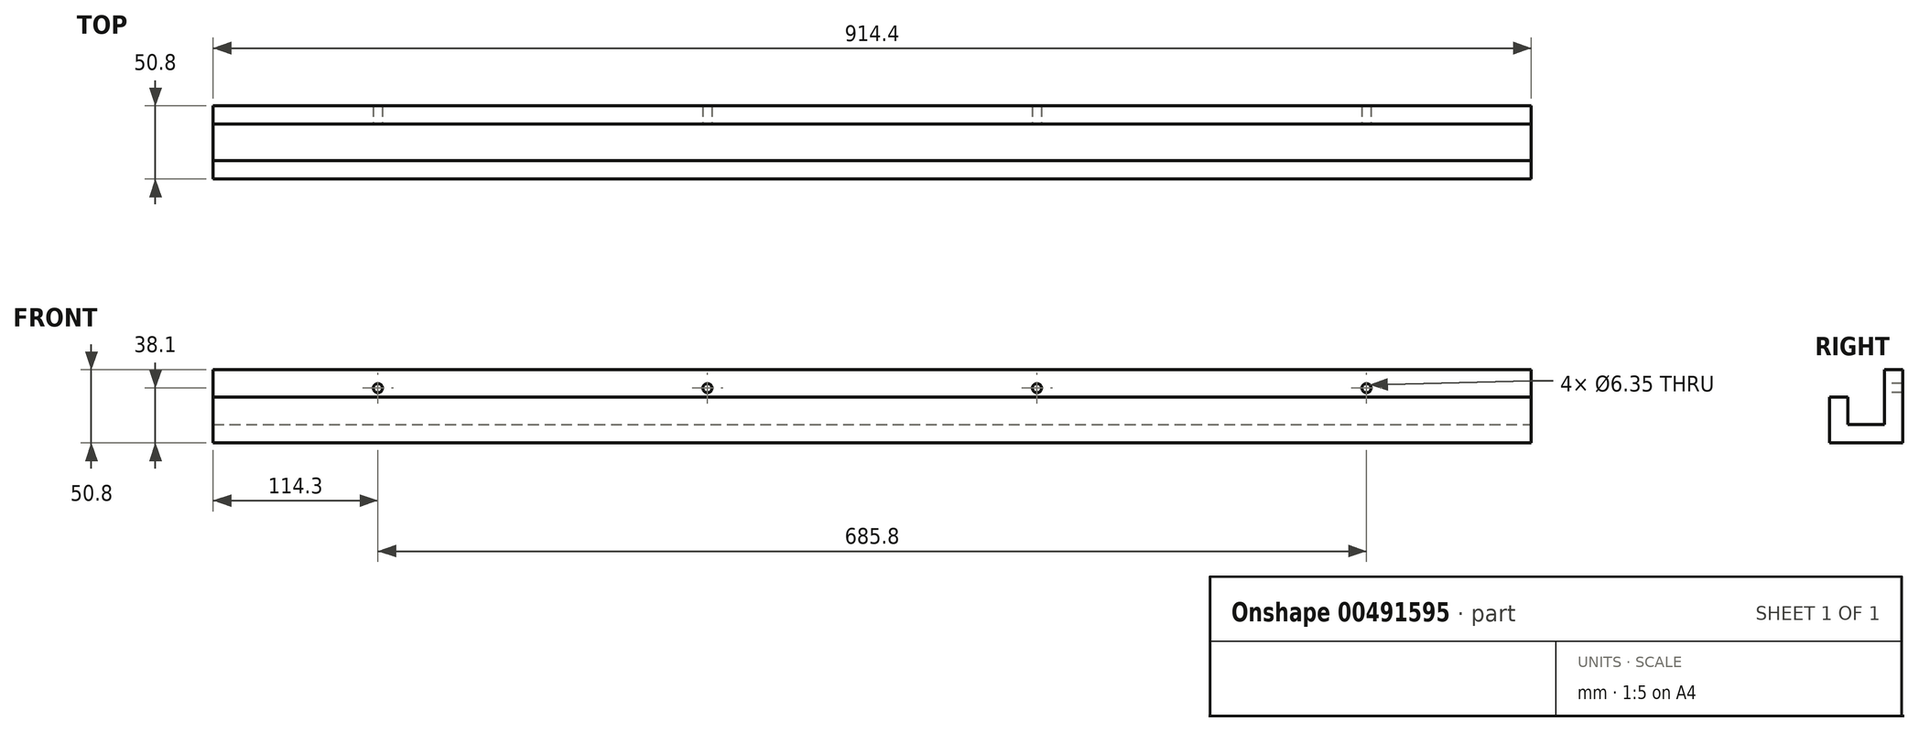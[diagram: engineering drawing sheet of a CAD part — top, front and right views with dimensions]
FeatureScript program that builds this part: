
annotation { "Feature Type Name" : "Feature", "Feature Type Description" : "" }
export const myFeature = defineFeature(function(context is Context, id is Id, definition is map)
    precondition{}
    {
        {
            var Q0;
            Q0=qCreatedBy(makeId("Front.planeOp"),FACE);
            var sketch = newSketch(context, id + "F0", { "sketchPlane" : qUnion([Q0])});
            skLineSegment(sketch, "E0.bottom", {"start": v(457.2, 25.4) * mm, "end": v(-457.2, 25.4) * mm});
            skLineSegment(sketch, "E0.top", {"start": v(457.2, -25.4) * mm, "end": v(-457.2, -25.4) * mm});
            skLineSegment(sketch, "E0.left", {"start": v(457.2, 25.4) * mm, "end": v(457.2, -25.4) * mm});
            skLineSegment(sketch, "E0.right", {"start": v(-457.2, 25.4) * mm, "end": v(-457.2, -25.4) * mm});
            skPoint(sketch, "E0.middle", {"position": v(0, 0) * mm});
            skSolve(sketch);
        }
        {
            var Q0;
            Q0=makeQuery(id+"F0.imprint","IMPRINT",FACE,{"disambiguationData":[TD([[makeQuery(id+"F0.imprint","IMPRINT",EDGE,{"derivedFrom":sQuery(id+"F0.wireOp",EDGE,"E0.bottom")}),1.0]])]});
            extrude(context, id + "F1", {"entities" : qUnion([Q0]), "depth" : 12.7 * mm});
        }
        {
            var Q0;
            Q0=makeQuery(id+"F1.opExtrude","CAP_FACE",FACE,{"disambiguationData":[OSD([sQuery(id+"F0.wireOp",EDGE,"E0.bottom"),sQuery(id+"F0.wireOp",EDGE,"E0.top"),sQuery(id+"F0.wireOp",EDGE,"E0.left"),sQuery(id+"F0.wireOp",EDGE,"E0.right")])],"isStart":false});
            var sketch = newSketch(context, id + "F2", { "sketchPlane" : qUnion([Q0])});
            skLineSegment(sketch, "E1.bottom", {"start": v(-457.2, -25.4) * mm, "end": v(457.2, -25.4) * mm});
            skLineSegment(sketch, "E1.top", {"start": v(-457.2, -12.7) * mm, "end": v(457.2, -12.7) * mm});
            skLineSegment(sketch, "E1.left", {"start": v(-457.2, -25.4) * mm, "end": v(-457.2, -12.7) * mm});
            skLineSegment(sketch, "E1.right", {"start": v(457.2, -25.4) * mm, "end": v(457.2, -12.7) * mm});
            skSolve(sketch);
        }
        {
            var Q0;
            Q0=makeQuery(id+"F2.imprint","IMPRINT",FACE,{"disambiguationData":[TD([[makeQuery(id+"F2.imprint","IMPRINT",EDGE,{"derivedFrom":sQuery(id+"F2.wireOp",EDGE,"E1.bottom")}),-1.0]])]});
            extrude(context, id + "F3", {"entities" : qUnion([Q0]), "operationType" : NewBodyOperationType.ADD, "depth" : 38.1 * mm});
        }
        {
            var Q0;
            Q0=makeQuery(id+"F3.opExtrude","SWEPT_FACE",FACE,{"disambiguationData":[OSD([sQuery(id+"F2.wireOp",EDGE,"E1.top")])]});
            var sketch = newSketch(context, id + "F4", { "sketchPlane" : qUnion([Q0])});
            skLineSegment(sketch, "E2.bottom", {"start": v(-457.2, -50.8) * mm, "end": v(457.2, -50.8) * mm});
            skLineSegment(sketch, "E2.top", {"start": v(-457.2, -38.1) * mm, "end": v(457.2, -38.1) * mm});
            skLineSegment(sketch, "E2.left", {"start": v(-457.2, -50.8) * mm, "end": v(-457.2, -38.1) * mm});
            skLineSegment(sketch, "E2.right", {"start": v(457.2, -50.8) * mm, "end": v(457.2, -38.1) * mm});
            skSolve(sketch);
        }
        {
            var Q0;
            Q0=makeQuery(id+"F4.imprint","IMPRINT",FACE,{"disambiguationData":[TD([[makeQuery(id+"F4.imprint","IMPRINT",EDGE,{"derivedFrom":sQuery(id+"F4.wireOp",EDGE,"E2.bottom")}),1.0]])]});
            extrude(context, id + "F5", {"entities" : qUnion([Q0]), "operationType" : NewBodyOperationType.ADD, "depth" : 19.05 * mm, "offsetDistance" : 25.4 * mm});
        }
        {
            var Q0;
            Q0=makeQuery(id+"F1.opExtrude","CAP_FACE",FACE,{"disambiguationData":[OSD([sQuery(id+"F0.wireOp",EDGE,"E0.bottom"),sQuery(id+"F0.wireOp",EDGE,"E0.top"),sQuery(id+"F0.wireOp",EDGE,"E0.left"),sQuery(id+"F0.wireOp",EDGE,"E0.right")])],"isStart":false});
            var sketch = newSketch(context, id + "F6", { "sketchPlane" : qUnion([Q0])});
            skCircle(sketch, "E3", {"center": v(-342.9, 12.7) * mm, "radius": 3.18 * mm});
            skCircle(sketch, "E4.1.0.0", {"center": v(-114.3, 12.7) * mm, "radius": 3.18 * mm});
            skCircle(sketch, "E4.2.0.0", {"center": v(114.3, 12.7) * mm, "radius": 3.18 * mm});
            skCircle(sketch, "E4.3.0.0", {"center": v(342.9, 12.7) * mm, "radius": 3.18 * mm});
            skLineSegment(sketch, "E4.direction1", {"start": v(-342.9, 12.7) * mm, "end": v(-114.3, 12.7) * mm, "construction": true});
            skSolve(sketch);
        }
        {
            var Q0;
            Q0=sQuery(id+"F6.wireOp",VERTEX,"E4.direction1.start");
            var Q1;
            Q1=sQuery(id+"F6.wireOp",VERTEX,"E4.1.0.0.center");
            var Q2;
            Q2=sQuery(id+"F6.wireOp",VERTEX,"E4.2.0.0.center");
            var Q3;
            Q3=sQuery(id+"F6.wireOp",VERTEX,"E4.3.0.0.center");
            var Q4;
            Q4=makeQuery(id+"F1.opExtrude","SWEPT_BODY",BODY,{"disambiguationData":[OSD([sQuery(id+"F0.wireOp",EDGE,"E0.bottom"),sQuery(id+"F0.wireOp",EDGE,"E0.top"),sQuery(id+"F0.wireOp",EDGE,"E0.left"),sQuery(id+"F0.wireOp",EDGE,"E0.right")])]});
            hole(context, id + "F7", {"style" : HoleStyle.SIMPLE, "endStyle" : HoleEndStyle.THROUGH, "holeDiameter" : 6.35 * mm, "isTappedThrough" : true, "tappedDepth" : 12.7 * mm, "tapClearance" : 3, "locations" : qUnion([Q0, Q1, Q2, Q3]), "scope" : qUnion([Q4])});
        }
    });
